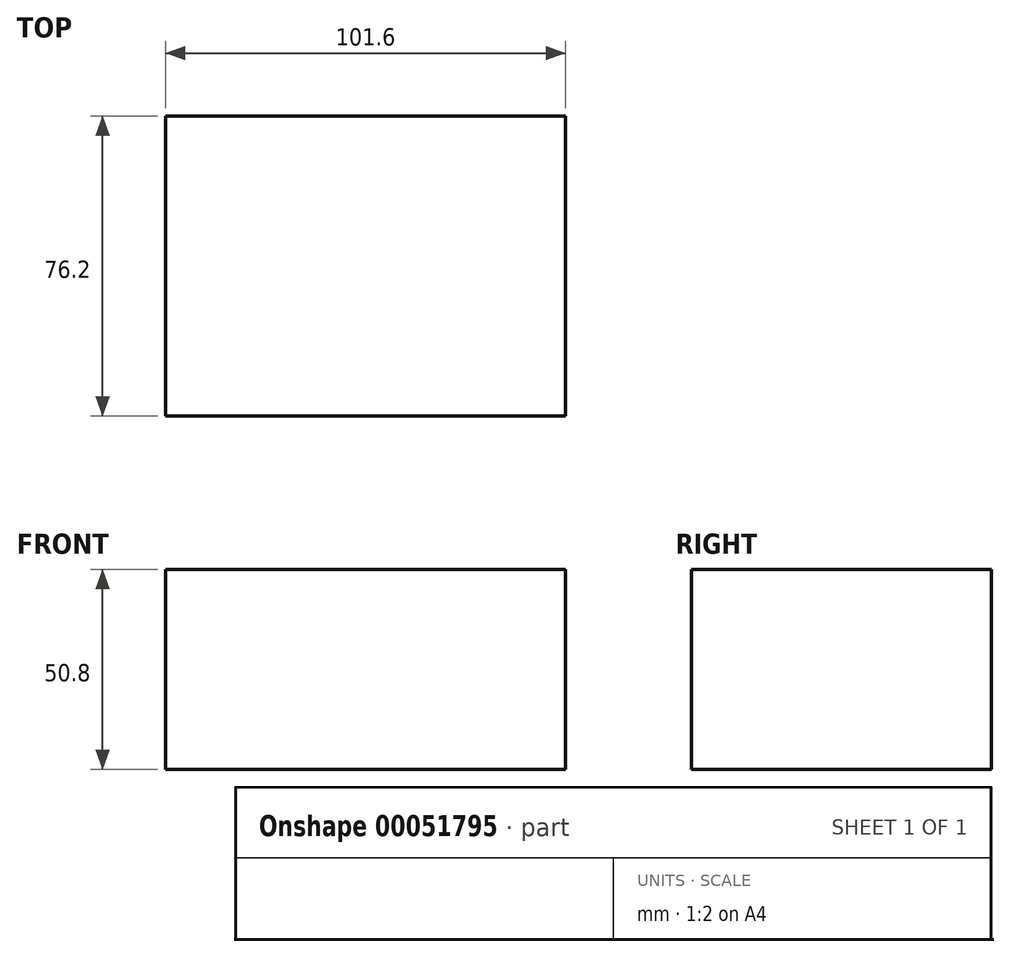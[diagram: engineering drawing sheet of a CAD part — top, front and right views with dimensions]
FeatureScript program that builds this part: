
annotation { "Feature Type Name" : "Feature", "Feature Type Description" : "" }
export const myFeature = defineFeature(function(context is Context, id is Id, definition is map)
    precondition{}
    {
        {
            var Q0;
            Q0=qCreatedBy(makeId("Top.planeOp"),FACE);
            var sketch = newSketch(context, id + "F0", { "sketchPlane" : qUnion([Q0])});
            skLineSegment(sketch, "E0.bottom", {"start": v(0, 0) * mm, "end": v(101.6, 0) * mm});
            skLineSegment(sketch, "E0.top", {"start": v(0, 76.2) * mm, "end": v(101.6, 76.2) * mm});
            skLineSegment(sketch, "E0.left", {"start": v(0, 0) * mm, "end": v(0, 76.2) * mm});
            skLineSegment(sketch, "E0.right", {"start": v(101.6, 0) * mm, "end": v(101.6, 76.2) * mm});
            skSolve(sketch);
        }
        {
            var Q0;
            Q0=makeQuery(id+"F0.imprint","IMPRINT",FACE,{"disambiguationData":[TD([[makeQuery(id+"F0.imprint","IMPRINT",EDGE,{"derivedFrom":sQuery(id+"F0.wireOp",EDGE,"E0.bottom")}),1.0]])]});
            extrude(context, id + "F1", {"entities" : qUnion([Q0]), "depth" : 50.8 * mm});
        }
    });
